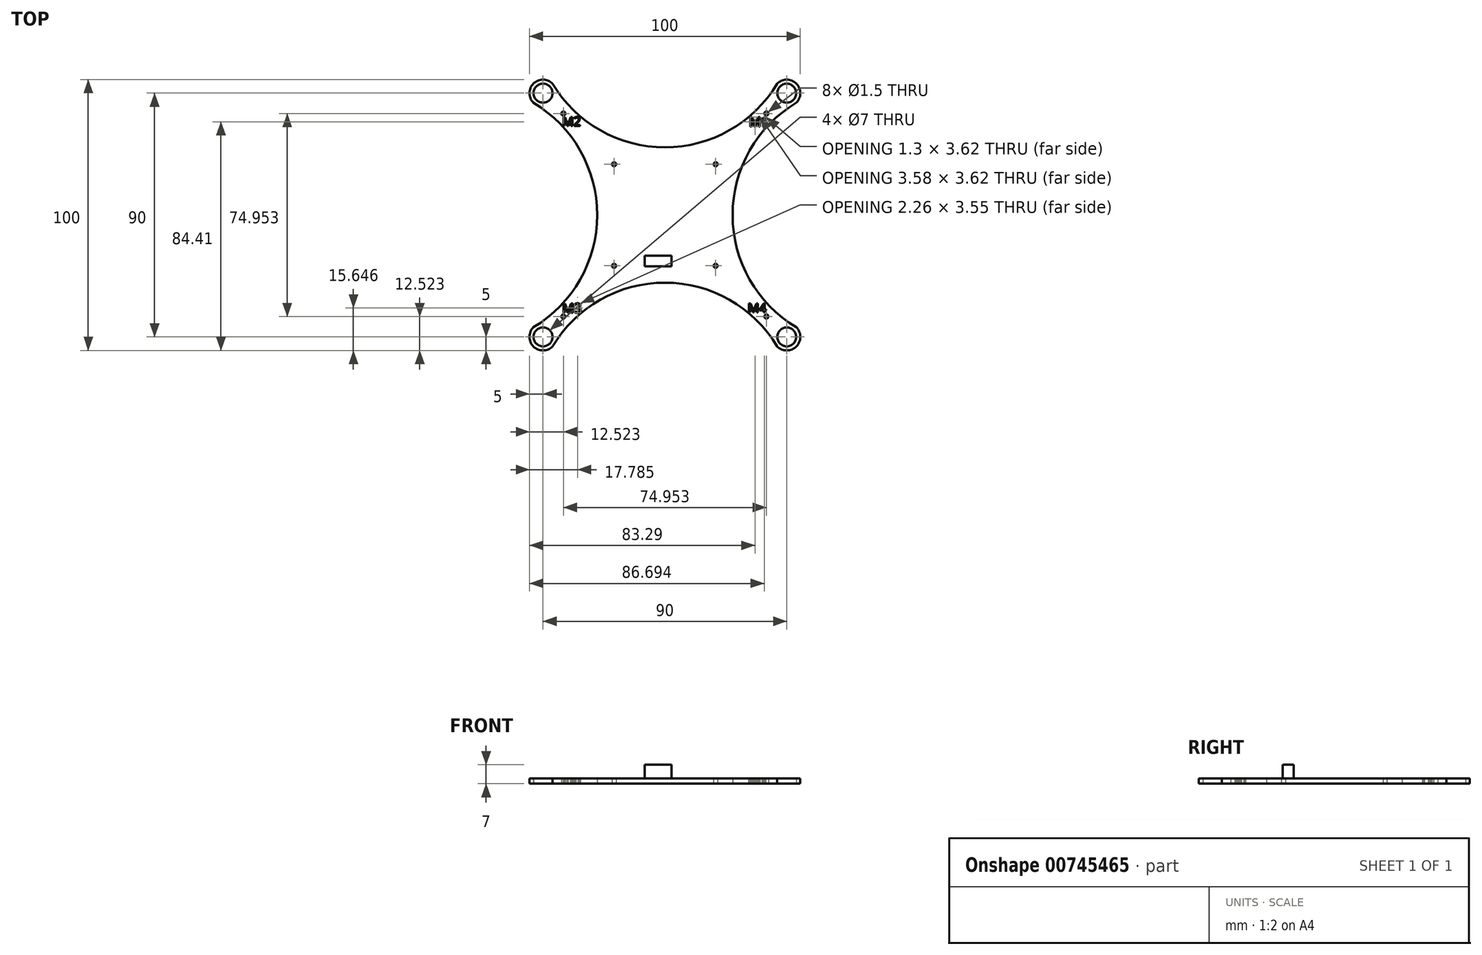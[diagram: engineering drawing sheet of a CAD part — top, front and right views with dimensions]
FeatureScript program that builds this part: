
annotation { "Feature Type Name" : "Feature", "Feature Type Description" : "" }
export const myFeature = defineFeature(function(context is Context, id is Id, definition is map)
    precondition{}
    {
        {
            var Q0;
            Q0=qCreatedBy(makeId("Top.planeOp"),FACE);
            var sketch = newSketch(context, id + "F0", { "sketchPlane" : qUnion([Q0])});
            skLineSegment(sketch, "E0", {"start": v(0, 0) * mm, "end": v(0, 25) * mm, "construction": true});
            skArc(sketch, "E1", {"start": v(0, 25) * mm, "mid": v(23.84, 31.3) * mm, "end": v(41.46, 48.54) * mm});
            skLineSegment(sketch, "E2", {"start": v(0, 0) * mm, "end": v(25, 0) * mm, "construction": true});
            skArc(sketch, "E3", {"start": v(25, 0) * mm, "mid": v(31.3, 23.84) * mm, "end": v(48.54, 41.46) * mm});
            skLineSegment(sketch, "E4", {"start": v(41.46, 48.54) * mm, "end": v(48.54, 41.46) * mm, "construction": true});
            skCircle(sketch, "E5", {"center": v(45, 45) * mm, "radius": 5 * mm});
            skCircle(sketch, "E6", {"center": v(45, 45) * mm, "radius": 3.5 * mm});
            skArc(sketch, "E7.1.0", {"start": v(0, 25) * mm, "mid": v(-23.84, 31.3) * mm, "end": v(-41.46, 48.54) * mm});
            skCircle(sketch, "E7.1.1", {"center": v(-45, 45) * mm, "radius": 3.5 * mm});
            skArc(sketch, "E7.1.2", {"start": v(-25, 0) * mm, "mid": v(-31.3, 23.84) * mm, "end": v(-48.54, 41.46) * mm});
            skLineSegment(sketch, "E7.1.3", {"start": v(0, 0) * mm, "end": v(-25, 0) * mm, "construction": true});
            skCircle(sketch, "E7.1.4", {"center": v(-45, 45) * mm, "radius": 5 * mm});
            skLineSegment(sketch, "E7.1.6", {"start": v(-48.54, 41.46) * mm, "end": v(-41.46, 48.54) * mm, "construction": true});
            skArc(sketch, "E7.2.0", {"start": v(-25, 0) * mm, "mid": v(-31.3, -23.84) * mm, "end": v(-48.54, -41.46) * mm});
            skCircle(sketch, "E7.2.1", {"center": v(-45, -45) * mm, "radius": 3.5 * mm});
            skArc(sketch, "E7.2.2", {"start": v(0, -25) * mm, "mid": v(-23.84, -31.3) * mm, "end": v(-41.46, -48.54) * mm});
            skLineSegment(sketch, "E7.2.3", {"start": v(0, 0) * mm, "end": v(0, -25) * mm, "construction": true});
            skCircle(sketch, "E7.2.4", {"center": v(-45, -45) * mm, "radius": 5 * mm});
            skLineSegment(sketch, "E7.2.5", {"start": v(0, 0) * mm, "end": v(-25, 0) * mm, "construction": true});
            skLineSegment(sketch, "E7.2.6", {"start": v(-41.46, -48.54) * mm, "end": v(-48.54, -41.46) * mm, "construction": true});
            skArc(sketch, "E7.3.0", {"start": v(0, -25) * mm, "mid": v(23.84, -31.3) * mm, "end": v(41.46, -48.54) * mm});
            skCircle(sketch, "E7.3.1", {"center": v(45, -45) * mm, "radius": 3.5 * mm});
            skArc(sketch, "E7.3.2", {"start": v(25, 0) * mm, "mid": v(31.3, -23.84) * mm, "end": v(48.54, -41.46) * mm});
            skCircle(sketch, "E7.3.4", {"center": v(45, -45) * mm, "radius": 5 * mm});
            skLineSegment(sketch, "E7.3.5", {"start": v(0, 0) * mm, "end": v(0, -25) * mm, "construction": true});
            skLineSegment(sketch, "E7.3.6", {"start": v(48.54, -41.46) * mm, "end": v(41.46, -48.54) * mm, "construction": true});
            skPoint(sketch, "E7.center", {"position": v(0, 0) * mm});
            skLineSegment(sketch, "E8", {"start": v(0, 0) * mm, "end": v(45, 45) * mm, "construction": true});
            skCircle(sketch, "E9", {"center": v(37.48, 37.48) * mm, "radius": 0.75 * mm});
            skCircle(sketch, "E10", {"center": v(18.75, 18.75) * mm, "radius": 0.75 * mm});
            skCircle(sketch, "E11.1.0", {"center": v(-37.48, 37.48) * mm, "radius": 0.75 * mm});
            skCircle(sketch, "E11.1.1", {"center": v(-18.75, 18.75) * mm, "radius": 0.75 * mm});
            skCircle(sketch, "E11.2.0", {"center": v(-37.48, -37.48) * mm, "radius": 0.75 * mm});
            skCircle(sketch, "E11.2.1", {"center": v(-18.75, -18.75) * mm, "radius": 0.75 * mm});
            skCircle(sketch, "E11.3.0", {"center": v(37.48, -37.48) * mm, "radius": 0.75 * mm});
            skCircle(sketch, "E11.3.1", {"center": v(18.75, -18.75) * mm, "radius": 0.75 * mm});
            skSolve(sketch);
        }
        {
            var Q0;
            Q0=makeQuery(id+"F0.imprint","IMPRINT",FACE,{"disambiguationData":[TD([[makeQuery(id+"F0.imprint","IMPRINT",EDGE,{"derivedFrom":sQuery(id+"F0.wireOp",EDGE,"E9")}),-1.0]])]});
            var Q1;
            Q1=makeQuery(id+"F0.imprint","IMPRINT",FACE,{"disambiguationData":[TD([[makeQuery(id+"F0.imprint","IMPRINT",EDGE,{"derivedFrom":sQuery(id+"F0.wireOp",EDGE,"E7.2.1")}),-1.0]])]});
            var Q2;
            Q2=makeQuery(id+"F0.imprint","IMPRINT",FACE,{"disambiguationData":[TD([[makeQuery(id+"F0.imprint","IMPRINT",EDGE,{"derivedFrom":sQuery(id+"F0.wireOp",EDGE,"E7.3.1")}),-1.0]])]});
            var Q3;
            Q3=makeQuery(id+"F0.imprint","IMPRINT",FACE,{"disambiguationData":[TD([[makeQuery(id+"F0.imprint","IMPRINT",EDGE,{"derivedFrom":sQuery(id+"F0.wireOp",EDGE,"E6")}),-1.0]])]});
            var Q4;
            Q4=makeQuery(id+"F0.imprint","IMPRINT",FACE,{"disambiguationData":[TD([[makeQuery(id+"F0.imprint","IMPRINT",EDGE,{"derivedFrom":sQuery(id+"F0.wireOp",EDGE,"E7.1.1")}),-1.0]])]});
            extrude(context, id + "F1", {"entities" : qUnion([Q0, Q1, Q2, Q3, Q4]), "depth" : 2 * mm, "offsetDistance" : 25 * mm});
        }
        {
            var Q0;
            Q0=makeQuery(id+"F1.opExtrude","CAP_FACE",FACE,{"disambiguationData":[OSD([sQuery(id+"F0.wireOp",EDGE,"E1"),sQuery(id+"F0.wireOp",EDGE,"E3"),sQuery(id+"F0.wireOp",EDGE,"E5"),sQuery(id+"F0.wireOp",EDGE,"E6"),sQuery(id+"F0.wireOp",EDGE,"E7.1.0"),sQuery(id+"F0.wireOp",EDGE,"E7.1.1"),sQuery(id+"F0.wireOp",EDGE,"E7.1.2"),sQuery(id+"F0.wireOp",EDGE,"E7.1.4"),sQuery(id+"F0.wireOp",EDGE,"E7.2.0"),sQuery(id+"F0.wireOp",EDGE,"E7.2.1"),sQuery(id+"F0.wireOp",EDGE,"E7.2.2"),sQuery(id+"F0.wireOp",EDGE,"E7.2.4"),sQuery(id+"F0.wireOp",EDGE,"E7.3.0"),sQuery(id+"F0.wireOp",EDGE,"E7.3.1"),sQuery(id+"F0.wireOp",EDGE,"E7.3.2"),sQuery(id+"F0.wireOp",EDGE,"E7.3.4"),sQuery(id+"F0.wireOp",EDGE,"E9"),sQuery(id+"F0.wireOp",EDGE,"E10"),sQuery(id+"F0.wireOp",EDGE,"E11.1.0"),sQuery(id+"F0.wireOp",EDGE,"E11.1.1"),sQuery(id+"F0.wireOp",EDGE,"E11.2.0"),sQuery(id+"F0.wireOp",EDGE,"E11.2.1"),sQuery(id+"F0.wireOp",EDGE,"E11.3.0"),sQuery(id+"F0.wireOp",EDGE,"E11.3.1")])],"isStart":false});
            var sketch = newSketch(context, id + "F2", { "sketchPlane" : qUnion([Q0])});
            skLineSegment(sketch, "E12.bottom", {"start": v(-7.5, -15) * mm, "end": v(2.5, -15) * mm});
            skLineSegment(sketch, "E12.top", {"start": v(-7.5, -19) * mm, "end": v(2.5, -19) * mm});
            skLineSegment(sketch, "E12.left", {"start": v(-7.5, -15) * mm, "end": v(-7.5, -19) * mm});
            skLineSegment(sketch, "E12.right", {"start": v(2.5, -15) * mm, "end": v(2.5, -19) * mm});
            skSolve(sketch);
        }
        {
            var Q0;
            Q0=makeQuery(id+"F2.imprint","IMPRINT",FACE,{"disambiguationData":[TD([[makeQuery(id+"F2.imprint","IMPRINT",EDGE,{"derivedFrom":sQuery(id+"F2.wireOp",EDGE,"E12.bottom")}),-1.0]])]});
            extrude(context, id + "F3", {"entities" : qUnion([Q0]), "operationType" : NewBodyOperationType.ADD, "depth" : 5 * mm, "offsetDistance" : 25 * mm});
        }
        {
            var Q0;
            Q0=makeQuery(id+"F1.opExtrude","CAP_FACE",FACE,{"disambiguationData":[OSD([sQuery(id+"F0.wireOp",EDGE,"E1"),sQuery(id+"F0.wireOp",EDGE,"E3"),sQuery(id+"F0.wireOp",EDGE,"E5"),sQuery(id+"F0.wireOp",EDGE,"E6"),sQuery(id+"F0.wireOp",EDGE,"E7.1.0"),sQuery(id+"F0.wireOp",EDGE,"E7.1.1"),sQuery(id+"F0.wireOp",EDGE,"E7.1.2"),sQuery(id+"F0.wireOp",EDGE,"E7.1.4"),sQuery(id+"F0.wireOp",EDGE,"E7.2.0"),sQuery(id+"F0.wireOp",EDGE,"E7.2.1"),sQuery(id+"F0.wireOp",EDGE,"E7.2.2"),sQuery(id+"F0.wireOp",EDGE,"E7.2.4"),sQuery(id+"F0.wireOp",EDGE,"E7.3.0"),sQuery(id+"F0.wireOp",EDGE,"E7.3.1"),sQuery(id+"F0.wireOp",EDGE,"E7.3.2"),sQuery(id+"F0.wireOp",EDGE,"E7.3.4"),sQuery(id+"F0.wireOp",EDGE,"E9"),sQuery(id+"F0.wireOp",EDGE,"E10"),sQuery(id+"F0.wireOp",EDGE,"E11.1.0"),sQuery(id+"F0.wireOp",EDGE,"E11.1.1"),sQuery(id+"F0.wireOp",EDGE,"E11.2.0"),sQuery(id+"F0.wireOp",EDGE,"E11.2.1"),sQuery(id+"F0.wireOp",EDGE,"E11.3.0"),sQuery(id+"F0.wireOp",EDGE,"E11.3.1")])],"isStart":false});
            var sketch = newSketch(context, id + "F4", { "sketchPlane" : qUnion([Q0])});
            skText(sketch, "E13", { "text": "M3", "fontName": "OpenSans-Regular.ttf"});
            skText(sketch, "E14", { "text": "M4", "fontName": "OpenSans-Regular.ttf"});
            skText(sketch, "E15", { "text": "M1", "fontName": "OpenSans-Regular.ttf"});
            skText(sketch, "E16", { "text": "M2", "fontName": "OpenSans-Regular.ttf"});
            const initialGuessF4  = {"E13": [-0.03793, -0.03608, 1, 0, 0.00348], "E14": [0.03062, -0.03595, 1, 0, 0.00334], "E15": [0.031, 0.0326, 1, 0, 0.00365], "E16": [-0.03793, 0.0329, 1, 0, 0.00336]};
            skSetInitialGuess(sketch, initialGuessF4);
            skSolve(sketch);
        }
        {
            var Q0;
            Q0 = qSketchRegion(id + "F4", true);
            extrude(context, id + "F5", {"entities" : qUnion([Q0]), "operationType" : NewBodyOperationType.REMOVE, "oppositeDirection" : true, "depth" : 25 * mm, "offsetDistance" : 25 * mm});
        }
    });
